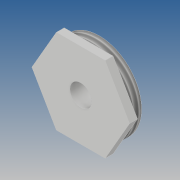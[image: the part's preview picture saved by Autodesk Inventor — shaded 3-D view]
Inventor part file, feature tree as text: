
AUTODESK INVENTOR PART (.ipt)
format: ipt  version: 2019 (Build 230136000, 136)  size: 118,272 bytes
history: native  units: mm
features: other x2, sketch x2, extrude x1
ambient origin geometry x8: Origin, YZ Plane, XZ Plane, XY Plane, X Axis, Y Axis, Z Axis, Center Point
bodies: Solide1 (feature_tree)
feature tree (5):
  other  "Révolution1"
  extrude  "Extrusion1"  Depth=1.5mm
  other  "Filetage1"
  sketch  "Esquisse1"
  sketch  "Esquisse2"
